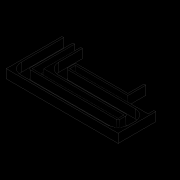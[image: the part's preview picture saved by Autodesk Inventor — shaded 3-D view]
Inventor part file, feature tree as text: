
AUTODESK INVENTOR PART (.ipt)
format: ipt  version: 2022 (Build 260153000, 153)  size: 199,168 bytes
history: native  units: in
note: dims shown in document units (in); Inventor stores cm internally (conversion verified against a paired STEP export)
features: fillet x2, extrude x1, sketch x1
ambient origin geometry x8: Origin, YZ Plane, XZ Plane, XY Plane, X Axis, Y Axis, Z Axis, Center Point
bodies: Solid1 (feature_tree)
feature tree (4):
  extrude  "Extrusion1"  Depth=1.378in
  fillet  "Fillet1"  Radius=0.1575in
  fillet  "Fillet2"  Radius=0.1575in
  sketch  "Sketch1"  dims[d10=4.7244in d13=1.378in d14=0.1575in d15=0.1575in d16=0.1575in d17=0.4921in d20=0.7874in d21=0.1575in d23=0.1575in d25=0.1575in d26=0.7874in d28=0.748in d29=0.0in d31=0.1575in d32=0.1575in d34=0.4921in d35=0.1575in d36=0.7874in d37=0.9449in d38=0.1575in d43=0.1575in d44=0.1575in d46=0.7874in d47=0.1575in d48=0.7874in d49=0.1575in d50=5.2362in d51=6.811in]
